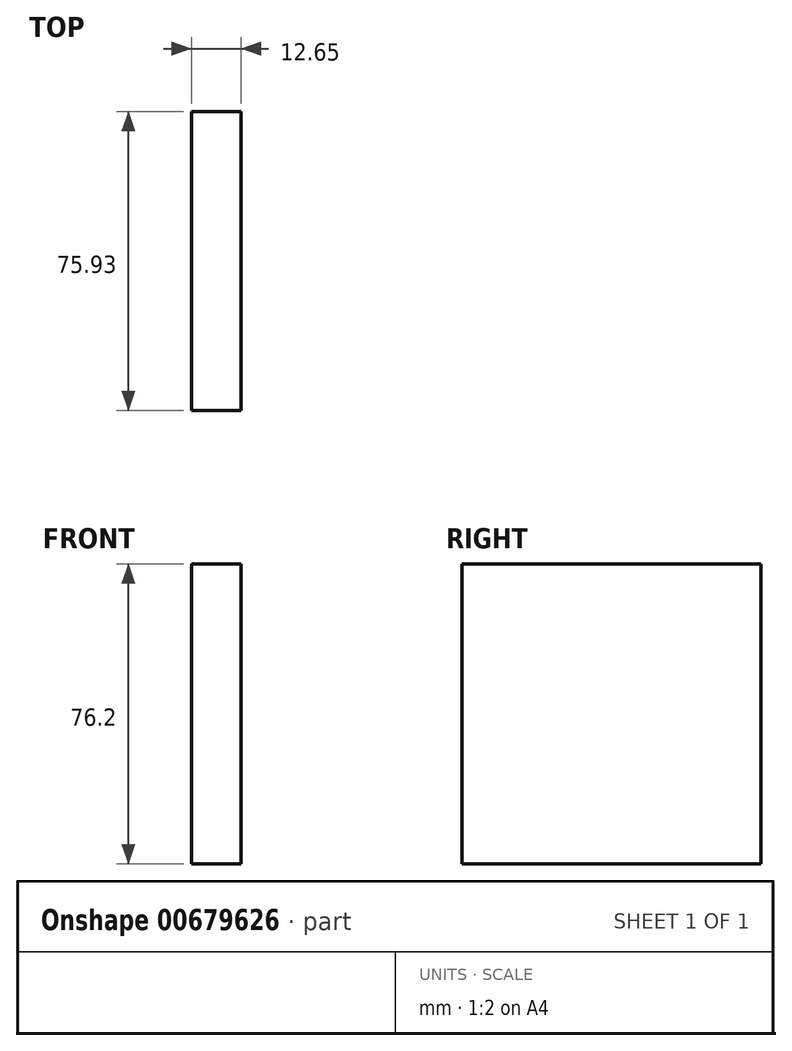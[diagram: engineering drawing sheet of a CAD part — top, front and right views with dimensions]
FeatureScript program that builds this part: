
annotation { "Feature Type Name" : "Feature", "Feature Type Description" : "" }
export const myFeature = defineFeature(function(context is Context, id is Id, definition is map)
    precondition{}
    {
        {
            var Q0;
            Q0=qCreatedBy(makeId("Top.planeOp"),FACE);
            var sketch = newSketch(context, id + "F0", { "sketchPlane" : qUnion([Q0])});
            skLineSegment(sketch, "E0.bottom", {"start": v(0, 0) * mm, "end": v(12.65, 0) * mm});
            skLineSegment(sketch, "E0.top", {"start": v(0, 75.93) * mm, "end": v(12.65, 75.93) * mm});
            skLineSegment(sketch, "E0.left", {"start": v(0, 0) * mm, "end": v(0, 75.93) * mm});
            skLineSegment(sketch, "E0.right", {"start": v(12.65, 0) * mm, "end": v(12.65, 75.93) * mm});
            skSolve(sketch);
        }
        {
            var Q0;
            Q0=makeQuery(id+"F0.imprint","IMPRINT",FACE,{"disambiguationData":[TD([[makeQuery(id+"F0.imprint","IMPRINT",EDGE,{"derivedFrom":sQuery(id+"F0.wireOp",EDGE,"E0.bottom")}),1.0]])]});
            extrude(context, id + "F1", {"entities" : qUnion([Q0]), "oppositeDirection" : true, "depth" : 76.2 * mm, "offsetDistance" : 25.4 * mm});
        }
    });
